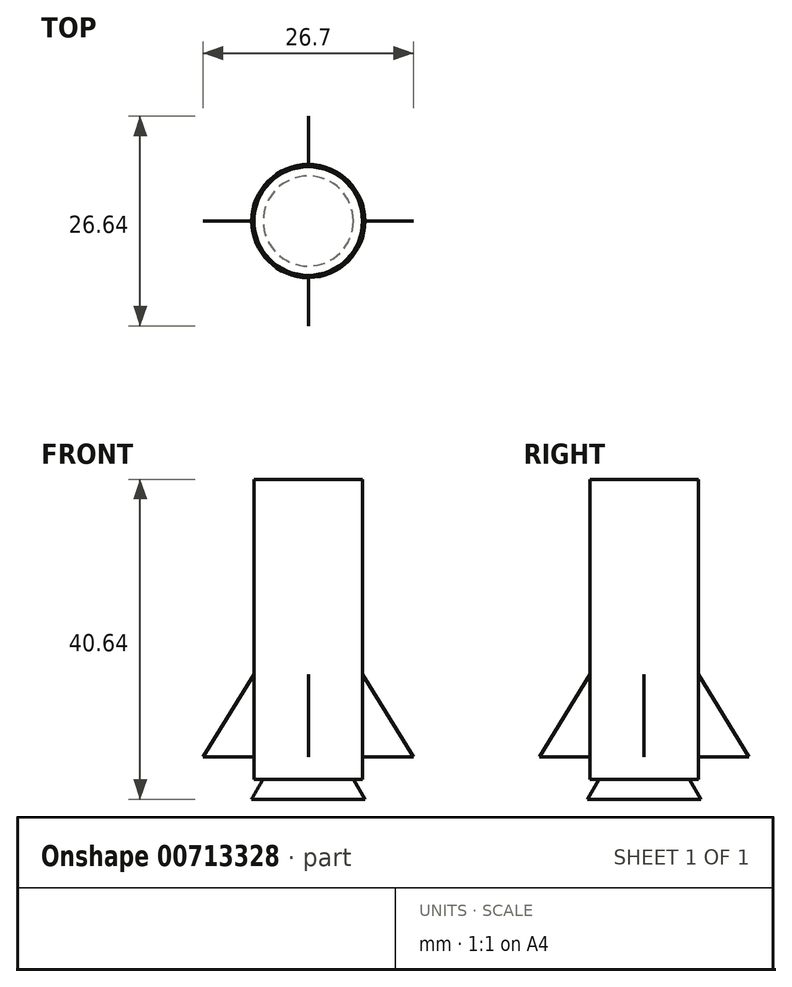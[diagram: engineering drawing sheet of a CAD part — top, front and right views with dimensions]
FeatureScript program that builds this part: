
annotation { "Feature Type Name" : "Feature", "Feature Type Description" : "" }
export const myFeature = defineFeature(function(context is Context, id is Id, definition is map)
    precondition{}
    {
        {
            var Q0;
            Q0=qCreatedBy(makeId("Top.planeOp"),FACE);
            var sketch = newSketch(context, id + "F0", { "sketchPlane" : qUnion([Q0])});
            skCircle(sketch, "E0", {"center": v(0, 0) * mm, "radius": 6.9 * mm});
            skSolve(sketch);
        }
        {
            var Q0;
            Q0=qSketchRegion(id+"F0",true);
            extrude(context, id + "F1", {"entities" : qUnion([Q0]), "oppositeDirection" : true, "depth" : 38.1 * mm, "offsetDistance" : 25.4 * mm});
        }
        {
            var Q0;
            Q0=makeQuery(id+"F1.opExtrude","CAP_FACE",FACE,{"disambiguationData":[OSD([sQuery(id+"F0.wireOp",EDGE,"E0")])],"isStart":false});
            var sketch = newSketch(context, id + "F2", { "sketchPlane" : qUnion([Q0])});
            skCircle(sketch, "E1", {"center": v(0, 0) * mm, "radius": 5.72 * mm});
            skLineSegment(sketch, "E2", {"start": v(-5.72, 0) * mm, "end": v(5.72, 0) * mm});
            skSolve(sketch);
        }
        {
            var Q0;
            Q0=qSketchRegion(id+"F2",true);
            extrude(context, id + "F3", {"entities" : qUnion([Q0]), "operationType" : NewBodyOperationType.ADD, "depth" : 2.54 * mm, "offsetDistance" : 25.4 * mm, "hasDraft" : true, "draftAngle" : 30 * degree});
        }
        {
            var Q0;
            Q0=qCreatedBy(makeId("Front.planeOp"),FACE);
            var sketch = newSketch(context, id + "F4", { "sketchPlane" : qUnion([Q0])});
            skLineSegment(sketch, "E3", {"start": v(6.91, -24.78) * mm, "end": v(13.35, -35.26) * mm});
            skLineSegment(sketch, "E4", {"start": v(13.35, -35.26) * mm, "end": v(6.9, -35.26) * mm});
            skLineSegment(sketch, "E5", {"start": v(6.9, -35.26) * mm, "end": v(6.91, -24.78) * mm});
            skLineSegment(sketch, "E6.MirrorCS", {"start": v(-6.9, -35.26) * mm, "end": v(-6.91, -24.78) * mm});
            skLineSegment(sketch, "E7.MirrorCS", {"start": v(-6.91, -24.78) * mm, "end": v(-13.35, -35.26) * mm});
            skLineSegment(sketch, "E8.MirrorCS", {"start": v(-13.35, -35.26) * mm, "end": v(-6.9, -35.26) * mm});
            skSolve(sketch);
        }
        {
            var Q0;
            Q0=qSketchRegion(id+"F4",true);
            extrude(context, id + "F5", {"entities" : qUnion([Q0]), "depth" : 0.03 * mm, "offsetDistance" : 25.4 * mm});
        }
        {
            var Q0;
            Q0=qCreatedBy(makeId("Right.planeOp"),FACE);
            var sketch = newSketch(context, id + "F6", { "sketchPlane" : qUnion([Q0])});
            skLineSegment(sketch, "E9", {"start": v(6.9, -35.26) * mm, "end": v(6.9, -24.75) * mm});
            skLineSegment(sketch, "E10", {"start": v(6.9, -35.26) * mm, "end": v(13.32, -35.26) * mm});
            skLineSegment(sketch, "E11", {"start": v(13.32, -35.26) * mm, "end": v(6.9, -24.75) * mm});
            skLineSegment(sketch, "E12.MirrorCS", {"start": v(-6.9, -35.26) * mm, "end": v(-13.32, -35.26) * mm});
            skLineSegment(sketch, "E13.MirrorCS", {"start": v(-6.9, -35.26) * mm, "end": v(-6.9, -24.75) * mm});
            skLineSegment(sketch, "E14.MirrorCS", {"start": v(-13.32, -35.26) * mm, "end": v(-6.9, -24.75) * mm});
            skSolve(sketch);
        }
        {
            var Q0;
            Q0=qSketchRegion(id+"F6",true);
            extrude(context, id + "F7", {"entities" : qUnion([Q0]), "depth" : 0.03 * mm, "offsetDistance" : 25.4 * mm});
        }
        {
            var Q0;
            Q0=qCreatedBy(makeId("Front.planeOp"),FACE);
            var sketch = newSketch(context, id + "F8", { "sketchPlane" : qUnion([Q0])});
            skArc(sketch, "E15", {"start": v(0, 12.91) * mm, "mid": v(-4.51, 7.02) * mm, "end": v(-6.9, 0) * mm});
            skSolve(sketch);
        }
        {
            var Q0;
            Q0=sQuery(id+"F8.wireOp",EDGE,"E15");
            var Q1;
            Q1=makeQuery(id+"F1.opExtrude","CAP_EDGE",EDGE,{"disambiguationData":[OSD([sQuery(id+"F0.wireOp",EDGE,"E0")])],"isStart":true});
            revolve(context, id + "F9", {"bodyType" : ToolBodyType.SURFACE, "surfaceOperationType" : NewSurfaceOperationType.NEW, "surfaceEntities" : qUnion([Q0]), "axis" : qUnion([Q1]), "revolveType" : RevolveType.FULL});
        }
    });
